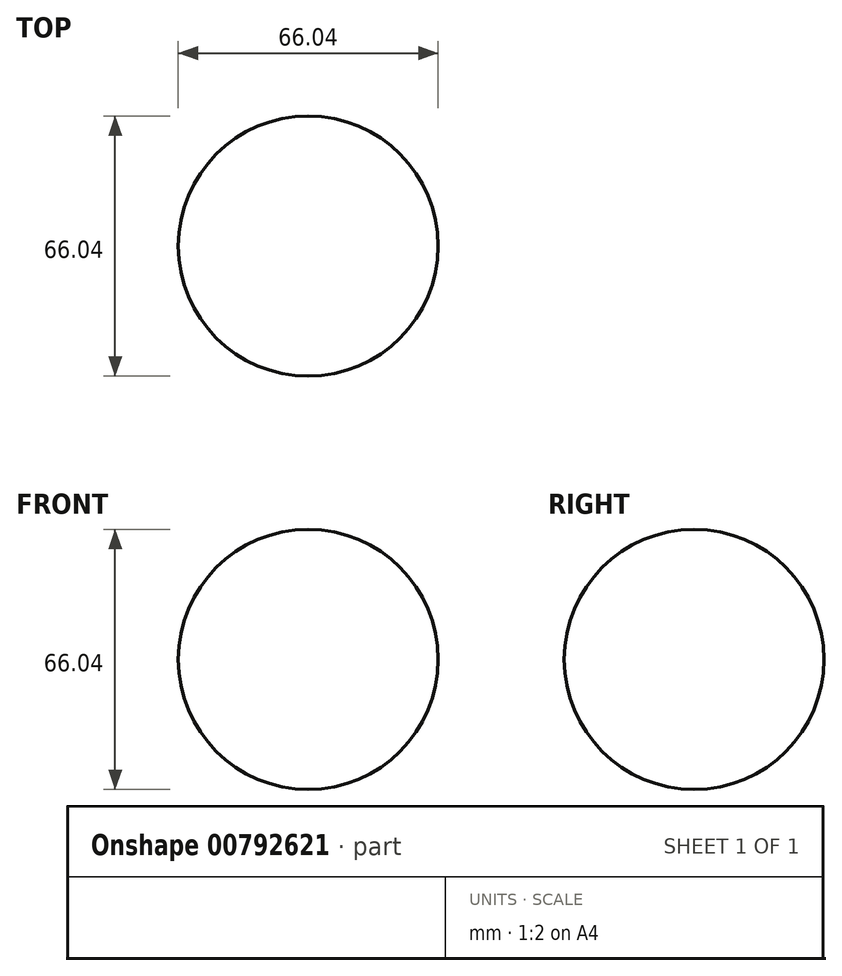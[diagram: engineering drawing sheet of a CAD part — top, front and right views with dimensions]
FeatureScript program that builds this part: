
annotation { "Feature Type Name" : "Feature", "Feature Type Description" : "" }
export const myFeature = defineFeature(function(context is Context, id is Id, definition is map)
    precondition{}
    {
        {
            var Q0;
            Q0=qCreatedBy(makeId("Front.planeOp"),FACE);
            var sketch = newSketch(context, id + "F0", { "sketchPlane" : qUnion([Q0])});
            skArc(sketch, "E0", {"start": v(0, 33.02) * mm, "mid": v(-33.02, 0) * mm, "end": v(0, -33.02) * mm});
            skLineSegment(sketch, "E1", {"start": v(0, 33.02) * mm, "end": v(0, -33.02) * mm});
            skSolve(sketch);
        }
        {
            var Q0;
            Q0=makeQuery(id+"F0.imprint","IMPRINT",FACE,{"disambiguationData":[TD([[makeQuery(id+"F0.imprint","IMPRINT",EDGE,{"derivedFrom":sQuery(id+"F0.wireOp",EDGE,"E0")}),1.0]])]});
            var Q1;
            Q1=sQuery(id+"F0.wireOp",EDGE,"E1");
            revolve(context, id + "F1", {"surfaceOperationType" : NewSurfaceOperationType.NEW, "entities" : qUnion([Q0]), "axis" : qUnion([Q1]), "revolveType" : RevolveType.FULL});
        }
    });
